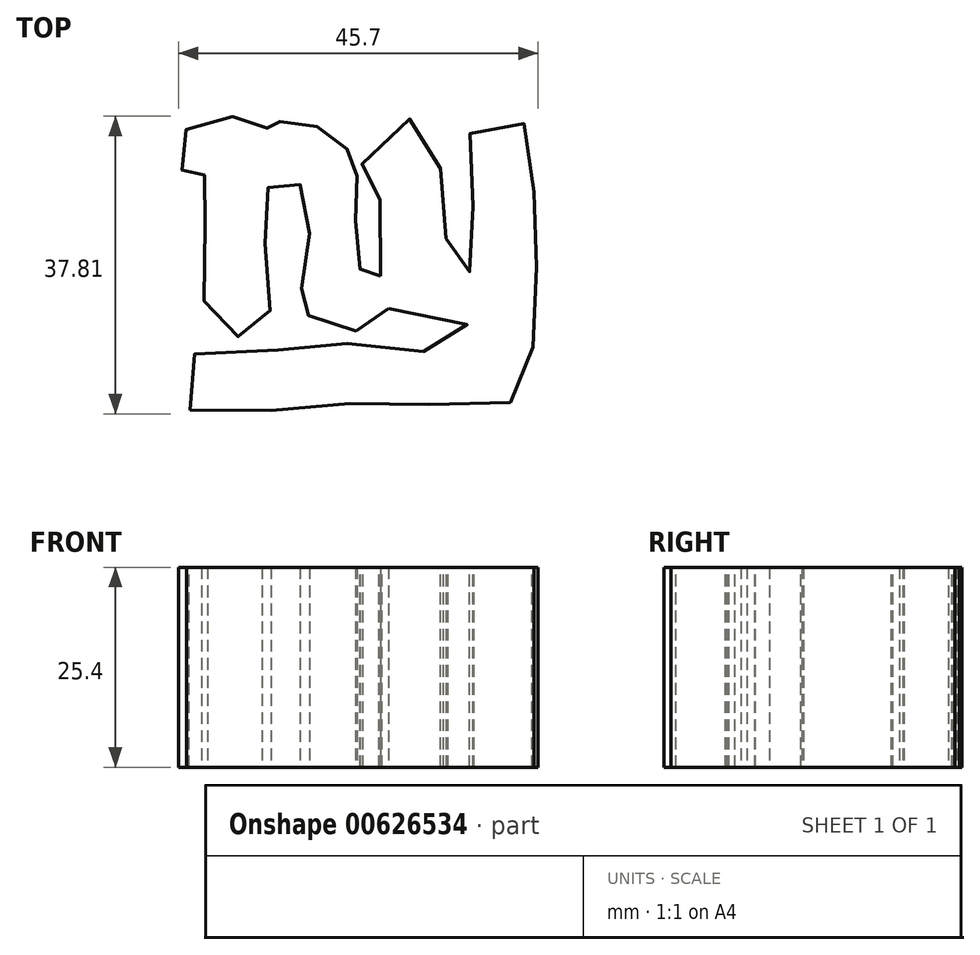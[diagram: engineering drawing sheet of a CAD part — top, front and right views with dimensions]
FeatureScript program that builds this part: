
annotation { "Feature Type Name" : "Feature", "Feature Type Description" : "" }
export const myFeature = defineFeature(function(context is Context, id is Id, definition is map)
    precondition{}
    {
        {
            var Q0;
            Q0=qCreatedBy(makeId("Top.planeOp"),FACE);
            var sketch = newSketch(context, id + "F0", { "sketchPlane" : qUnion([Q0])});
            skFitSpline(sketch, "E0", {"points": [v(-56.24, 53.46) * mm, v(-56.64, 47.38) * mm, v(-54.2, 47.17) * mm, v(-53.6, 29.12) * mm, v(-46.5, 28.31) * mm, v(-46.5, 45.14) * mm, v(-42.04, 45.96) * mm, v(-41.84, 33.38) * mm, v(-41.23, 29.53) * mm, v(-31.9, 28.31) * mm, v(-31.9, 34.4) * mm, v(-34.13, 34.8) * mm, v(-34.94, 44.54) * mm, v(-35.35, 49.2) * mm, v(-39.2, 53.05) * mm, v(-45.08, 53.87) * mm, v(-46.1, 53.05) * mm, v(-46.9, 53.66) * mm, v(-56.24, 53.46) * mm]});
            skFitSpline(sketch, "E1", {"points": [v(-34.13, 53.46) * mm, v(-23.79, 53.46) * mm, v(-23.99, 50.22) * mm, v(-24.2, 45.96) * mm, v(-23.79, 40.68) * mm, v(-23.58, 38.25) * mm, v(-23.58, 34.8) * mm, v(-20.74, 34.8) * mm, v(-20.14, 38.45) * mm, v(-20.14, 42.3) * mm, v(-20.14, 45.96) * mm, v(-20.34, 51.63) * mm, v(-20.54, 53.46) * mm, v(-18.1, 53.46) * mm, v(-13.04, 53.46) * mm, v(-12.43, 47.78) * mm, v(-12.43, 44.54) * mm, v(-12.43, 38.45) * mm, v(-12.02, 34.8) * mm, v(-12.02, 29.12) * mm, v(-12.63, 23.24) * mm, v(-12.63, 20.2) * mm, v(-17.1, 17.97) * mm, v(-23.18, 17.97) * mm, v(-28.25, 18.17) * mm, v(-34.13, 18.37) * mm, v(-39.2, 17.77) * mm, v(-45.08, 17.36) * mm, v(-50.36, 17.16) * mm, v(-56.24, 17.56) * mm, v(-56.24, 21.42) * mm, v(-56.24, 24.05) * mm, v(-51.37, 25.07) * mm, v(-45.08, 25.07) * mm, v(-42.04, 25.07) * mm, v(-36.97, 25.88) * mm, v(-31.9, 25.27) * mm, v(-26.63, 24.86) * mm, v(-20.95, 25.47) * mm, v(-20.34, 27.9) * mm, v(-27.44, 28.51) * mm, v(-30.92, 30.3) * mm, v(-30.93, 32.36) * mm, v(-31.9, 34.4) * mm, v(-31.9, 39.87) * mm, v(-31.9, 44.54) * mm, v(-31.9, 45.96) * mm, v(-34.13, 45.96) * mm, v(-34.13, 50.82) * mm, v(-34.13, 53.46) * mm]});
            skSolve(sketch);
        }
        {
            var Q0;
            Q0 = qSketchRegion(id + "F0", true);
            extrude(context, id + "F1", {"entities" : qUnion([Q0]), "depth" : 25.4 * mm, "offsetDistance" : 25.4 * mm});
        }
    });
